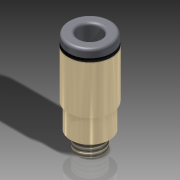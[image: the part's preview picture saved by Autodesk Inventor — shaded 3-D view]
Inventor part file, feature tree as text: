
AUTODESK INVENTOR PART (.ipt)
format: ipt  version: 2011 (Build 150239000, 239)  size: 154,112 bytes
history: native  units: in
note: dims shown in document units (in); Inventor stores cm internally (conversion verified against a paired STEP export)
features: other x1, imported_body x1, thread x1
ambient origin geometry x8: Origin, YZ Plane, XZ Plane, XY Plane, X Axis, Y Axis, Z Axis, Center Point
feature tree (3):
  other  "Port"
  imported_body  "Base1"
  thread  "Thread1"  [1 undecoded]
note: 1 required parameter value undecoded (feature->parameter linkage not recoverable at this tier; creation-order binding heuristic only, values carry confidence <= 0.55)
